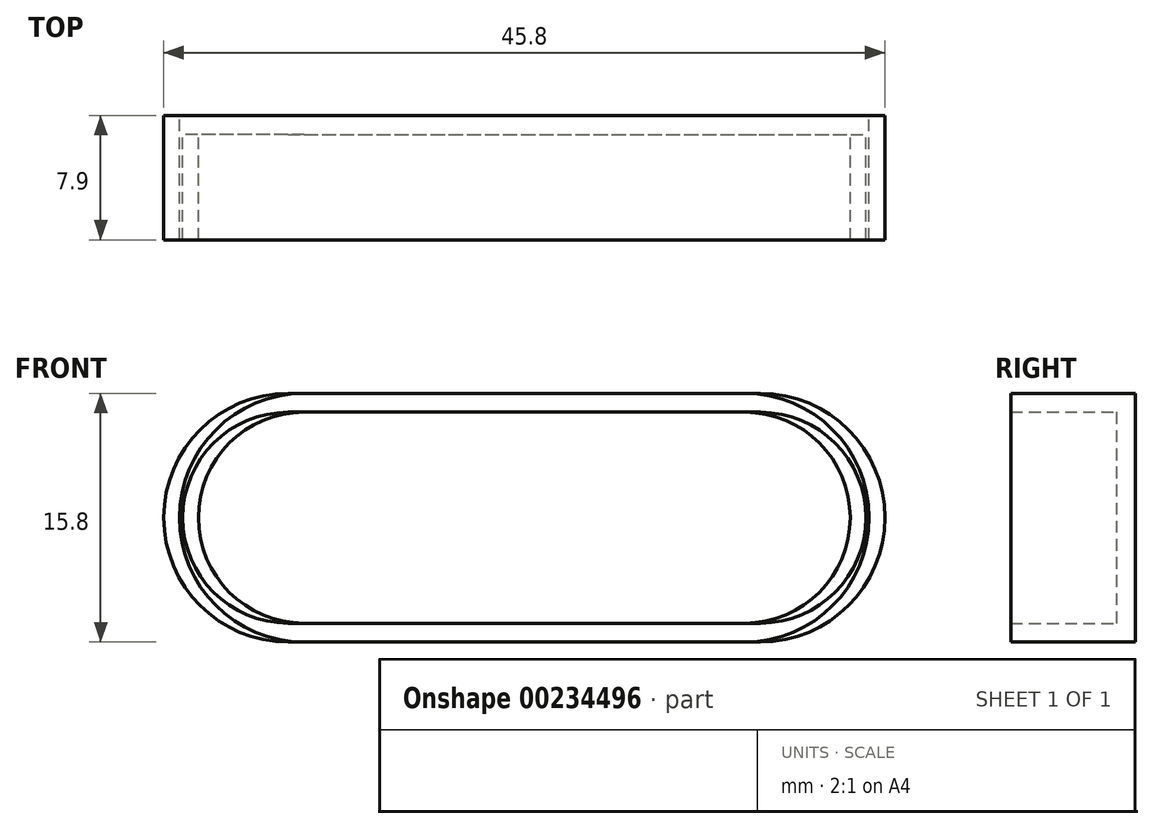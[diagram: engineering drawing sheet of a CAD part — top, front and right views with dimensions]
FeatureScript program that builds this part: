
annotation { "Feature Type Name" : "Feature", "Feature Type Description" : "" }
export const myFeature = defineFeature(function(context is Context, id is Id, definition is map)
    precondition{}
    {
        {
            var Q0;
            Q0=qCreatedBy(makeId("Front.planeOp"),FACE);
            var sketch = newSketch(context, id + "F0", { "sketchPlane" : qUnion([Q0])});
            skLineSegment(sketch, "E0", {"start": v(-14, 0) * mm, "end": v(14, 0) * mm});
            skArc(sketch, "E1.0.startCap", {"start": v(-14, -7.9) * mm, "mid": v(-21.9, 0) * mm, "end": v(-14, 7.9) * mm});
            skArc(sketch, "E1.0.endCap", {"start": v(14, 7.9) * mm, "mid": v(21.9, 0) * mm, "end": v(14, -7.9) * mm});
            skLineSegment(sketch, "E1.0.left", {"start": v(-14, 7.9) * mm, "end": v(14, 7.9) * mm});
            skLineSegment(sketch, "E1.0.right", {"start": v(-14, -7.9) * mm, "end": v(14, -7.9) * mm});
            skSolve(sketch);
        }
        {
            var Q0;
            Q0 = qSketchRegion(id + "F0", true);
            extrude(context, id + "F1", {"entities" : qUnion([Q0]), "depth" : 7.9 * mm});
        }
        {
            var Q0;
            Q0=makeQuery(id+"F1.opExtrude","CAP_FACE",FACE,{"disambiguationData":[OSD([sQuery(id+"F0.wireOp",EDGE,"E1.0.startCap"),sQuery(id+"F0.wireOp",EDGE,"E1.0.endCap"),sQuery(id+"F0.wireOp",EDGE,"E1.0.left"),sQuery(id+"F0.wireOp",EDGE,"E1.0.right")])],"isStart":false});
            shell(context, id + "F2", {"entities" : qUnion([Q0]), "thickness" : 1.2 * mm});
        }
        {
            var Q0;
            Q0=qCreatedBy(makeId("Front.planeOp"),FACE);
            var sketch = newSketch(context, id + "F3", { "sketchPlane" : qUnion([Q0])});
            skLineSegment(sketch, "E2", {"start": v(-15, 0) * mm, "end": v(15, 0) * mm});
            skArc(sketch, "E3.0.startCap", {"start": v(-15, -7.9) * mm, "mid": v(-22.9, 0) * mm, "end": v(-15, 7.9) * mm});
            skArc(sketch, "E3.0.endCap", {"start": v(15, 7.9) * mm, "mid": v(22.9, 0) * mm, "end": v(15, -7.9) * mm});
            skLineSegment(sketch, "E3.0.left", {"start": v(-15, 7.9) * mm, "end": v(15, 7.9) * mm});
            skLineSegment(sketch, "E3.0.right", {"start": v(-15, -7.9) * mm, "end": v(15, -7.9) * mm});
            skSolve(sketch);
        }
        {
            var Q0;
            Q0 = qSketchRegion(id + "F3", true);
            extrude(context, id + "F4", {"entities" : qUnion([Q0]), "depth" : 7.9 * mm});
        }
        {
            var Q0;
            Q0=makeQuery(id+"F4.opExtrude","CAP_FACE",FACE,{"disambiguationData":[OSD([sQuery(id+"F3.wireOp",EDGE,"E3.0.startCap"),sQuery(id+"F3.wireOp",EDGE,"E3.0.endCap"),sQuery(id+"F3.wireOp",EDGE,"E3.0.left"),sQuery(id+"F3.wireOp",EDGE,"E3.0.right")])],"isStart":false});
            shell(context, id + "F5", {"entities" : qUnion([Q0]), "thickness" : 1.2 * mm});
        }
    });
